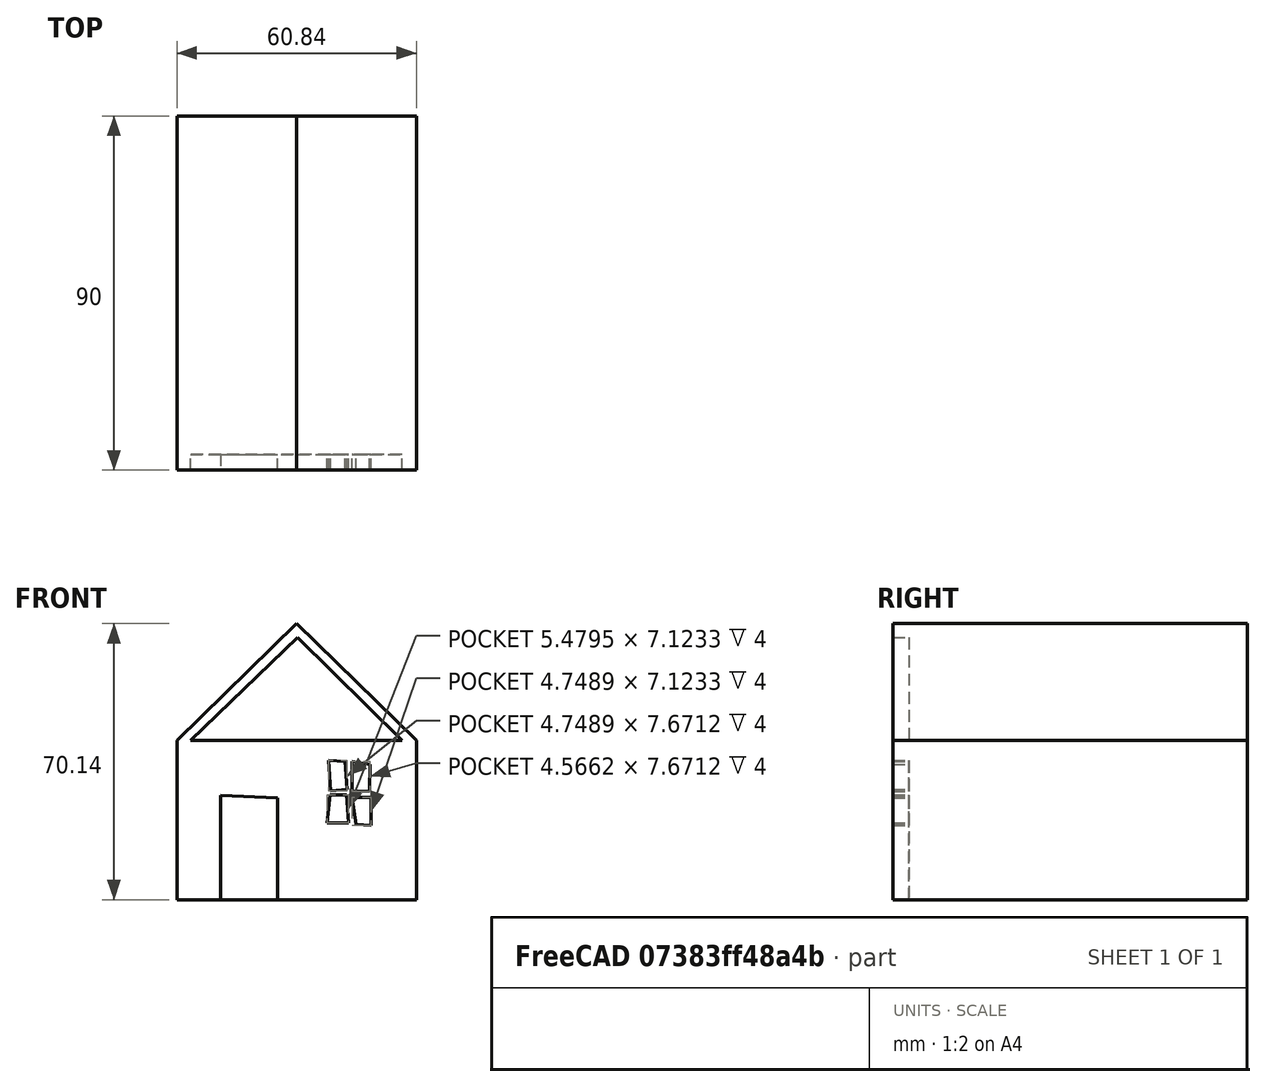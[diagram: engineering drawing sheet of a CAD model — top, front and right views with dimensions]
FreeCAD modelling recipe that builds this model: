
FCSTD DOCUMENT  (FreeCAD 0.21R33694 (Git))
Label: OJT1_T017_R02_caseta
License: All rights reserved
LicenseURL: http://en.wikipedia.org/wiki/All_rights_reserved
objects: PartDesign::SubShapeBinder×5, Sketcher::SketchObject×2, PartDesign::Pad×1, PartDesign::Pocket×1, PartDesign::Body×1
note: 12 computed .brp shape members not serialized (recipe doc carries the construction recipe); baked Part::Feature solids carry a one-line shape summary decoded from their .brp

FEATURE [Sketcher::SketchObject] Sketch
  FullyConstrained = false
  MapMode = 5
  Support = -> [XY_Plane]
  sketch-geometry (5):
    g0: LineSegment StartX=0 StartY=29.646 StartZ=0 EndX=-30.4204 EndY=0 EndZ=0
    g1: LineSegment StartX=-30.4204 StartY=0 StartZ=0 EndX=-30.4204 EndY=-40.4867 EndZ=0
    g2: LineSegment StartX=-30.4204 StartY=-40.4867 StartZ=0 EndX=30.4204 EndY=-40.4867 EndZ=0
    g3: LineSegment StartX=30.4204 StartY=-40.4867 StartZ=0 EndX=30.4204 EndY=0 EndZ=0
    g4: LineSegment StartX=30.4204 StartY=0 StartZ=0 EndX=0 EndY=29.646 EndZ=0
  constraints (11):
    c: PointOnObject(g0,g-2)
    c: PointOnObject(g0,g-1)
    c: Coincident(g0,g1)
    c: Vertical(g1)
    c: Coincident(g1,g2)
    c: Horizontal(g2)
    c: Coincident(g2,g3)
    c: PointOnObject(g3,g-1)
    c: Vertical(g3)
    c: Coincident(g3,g4)
    c: Coincident(g4,g0)
FEATURE [PartDesign::Pad] Pad
  Direction = (0,0,1)
  Length = 90
  Length2 = 10
  Profile = -> Sketch
  ReferenceAxis = -> Sketch [N_Axis]
  Type = 0
FEATURE [Sketcher::SketchObject] Sketch001
  FullyConstrained = false
  MapMode = 5
  Placement = pos=(0,0,90) rot=(0,0,1;0rad)
  Support = -> [Pad]
  sketch-geometry (23):
    g0: LineSegment StartX=-19.3703 StartY=-13.9467 StartZ=0 EndX=-19.3703 EndY=-40.9403 EndZ=0
    g1: LineSegment StartX=-19.3703 StartY=-40.9403 StartZ=0 EndX=-4.86962 EndY=-40.9403 EndZ=0
    g2: LineSegment StartX=-4.86962 StartY=-40.9403 StartZ=0 EndX=-4.86962 EndY=-14.616 EndZ=0
    g3: LineSegment StartX=-4.86962 StartY=-14.616 StartZ=0 EndX=-19.3703 EndY=-13.9467 EndZ=0
    g4: LineSegment StartX=8.11109 StartY=-5.15465 StartZ=0 EndX=8.65904 EndY=-12.8259 EndZ=0
    g5: LineSegment StartX=8.65904 StartY=-12.8259 StartZ=0 EndX=12.86 EndY=-12.4606 EndZ=0
    g6: LineSegment StartX=12.86 StartY=-12.4606 StartZ=0 EndX=12.312 EndY=-5.3373 EndZ=0
    g7: LineSegment StartX=12.312 StartY=-5.3373 StartZ=0 EndX=8.11109 EndY=-5.15465 EndZ=0
    g8: LineSegment StartX=14.1385 StartY=-5.3373 StartZ=0 EndX=14.1385 EndY=-13.0085 EndZ=0
    g9: LineSegment StartX=14.1385 StartY=-13.0085 StartZ=0 EndX=18.5221 EndY=-12.8259 EndZ=0
    g10: LineSegment StartX=18.5221 StartY=-12.8259 StartZ=0 EndX=18.7047 EndY=-6.06789 EndZ=0
    g11: LineSegment StartX=18.7047 StartY=-6.06789 StartZ=0 EndX=14.1385 EndY=-5.3373 EndZ=0
    g12: LineSegment StartX=8.47639 StartY=-13.9218 StartZ=0 EndX=12.6773 EndY=-13.9218 EndZ=0
    g13: LineSegment StartX=12.6773 StartY=-13.9218 StartZ=0 EndX=13.2253 EndY=-21.0451 EndZ=0
    g14: LineSegment StartX=13.2253 StartY=-21.0451 StartZ=0 EndX=7.7458 EndY=-21.0451 EndZ=0
    g15: LineSegment StartX=7.7458 StartY=-21.0451 StartZ=0 EndX=8.47639 EndY=-13.9218 EndZ=0
    g16: LineSegment StartX=14.1385 StartY=-14.4697 StartZ=0 EndX=15.0517 EndY=-21.4104 EndZ=0
    g17: LineSegment StartX=15.0517 StartY=-21.4104 StartZ=0 EndX=18.8874 EndY=-21.593 EndZ=0
    g18: LineSegment StartX=18.8874 StartY=-21.593 StartZ=0 EndX=18.8874 EndY=-14.4697 EndZ=0
    g19: LineSegment StartX=18.8874 StartY=-14.4697 StartZ=0 EndX=14.1385 EndY=-14.4697 EndZ=0
    g20: LineSegment StartX=-26.9664 StartY=3.6e-15 StartZ=0 EndX=0.250248 EndY=26.0984 EndZ=0
    g21: LineSegment StartX=0.250248 StartY=26.0984 StartZ=0 EndX=26.7977 EndY=3.6e-15 EndZ=0
    g22: LineSegment StartX=26.7977 StartY=3.6e-15 StartZ=0 EndX=-26.9664 EndY=3.6e-15 EndZ=0
  constraints (33):
    c: Vertical(g0)
    c: Coincident(g0,g1)
    c: Horizontal(g1)
    c: Coincident(g1,g2)
    c: Vertical(g2)
    c: Coincident(g2,g3)
    c: Coincident(g3,g0)
    c: Coincident(g4,g5)
    c: Coincident(g5,g6)
    c: Coincident(g6,g7)
    c: Coincident(g7,g4)
    c: Vertical(g8)
    c: Coincident(g8,g9)
    c: Coincident(g9,g10)
    c: Coincident(g10,g11)
    c: Coincident(g11,g8)
    c: Horizontal(g12)
    c: Coincident(g12,g13)
    c: Coincident(g13,g14)
    c: Horizontal(g14)
    c: Coincident(g14,g15)
    c: Coincident(g15,g12)
    c: Coincident(g16,g17)
    c: Coincident(g17,g18)
    c: Vertical(g18)
    c: Coincident(g18,g19)
    c: Coincident(g19,g16)
    c: Horizontal(g19)
    c: PointOnObject(g20,g-1)
    c: Coincident(g20,g21)
    c: Coincident(g21,g22)
    c: Coincident(g22,g20)
    c: Horizontal(g22)
FEATURE [PartDesign::Pocket] Pocket
  BaseFeature = -> Pad
  Direction = (0,0,-1)
  Length = 4
  Length2 = 5
  Profile = -> Sketch001
  ReferenceAxis = -> Sketch001 [N_Axis]
  Type = 0
FEATURE [PartDesign::SubShapeBinder] Binder
  BindCopyOnChange = 0
  BindMode = 0
  ClaimChildren = false
  Context = -> Body [Binder.]
  Fuse = false
  MakeFace = true
  OffsetFill = false
  OffsetIntersection = false
  OffsetJoinType = 0
  OffsetOpenResult = false
  PartialLoad = false
  Relative = true
  Support = -> [Pocket[Face35]]
  _Version = 2
FEATURE [PartDesign::SubShapeBinder] Binder001
  BindCopyOnChange = 0
  BindMode = 0
  ClaimChildren = false
  Context = -> Body [Binder001.]
  Fuse = false
  MakeFace = true
  OffsetFill = false
  OffsetIntersection = false
  OffsetJoinType = 0
  OffsetOpenResult = false
  PartialLoad = false
  Relative = true
  Support = -> [Pocket[Face2]]
  _Version = 2
FEATURE [PartDesign::SubShapeBinder] Binder002
  BindCopyOnChange = 0
  BindMode = 0
  ClaimChildren = false
  Context = -> Body [Binder002.]
  Fuse = false
  MakeFace = true
  OffsetFill = false
  OffsetIntersection = false
  OffsetJoinType = 0
  OffsetOpenResult = false
  PartialLoad = false
  Relative = true
  Support = -> [Pocket[Face1]]
  _Version = 2
FEATURE [PartDesign::SubShapeBinder] Binder003
  BindCopyOnChange = 0
  BindMode = 0
  ClaimChildren = false
  Context = -> Body [Binder003.]
  Fuse = false
  MakeFace = true
  OffsetFill = false
  OffsetIntersection = false
  OffsetJoinType = 0
  OffsetOpenResult = false
  PartialLoad = false
  Relative = true
  Support = -> [Pocket[Face30]]
  _Version = 2
FEATURE [PartDesign::SubShapeBinder] Binder004
  BindCopyOnChange = 0
  BindMode = 0
  ClaimChildren = false
  Context = -> Body [Binder004.]
  Fuse = false
  MakeFace = true
  OffsetFill = false
  OffsetIntersection = false
  OffsetJoinType = 0
  OffsetOpenResult = false
  PartialLoad = false
  Relative = true
  Support = -> [Pocket[Face33,Face34,Face31,Face32]]
  _Version = 2
FEATURE [PartDesign::Body] Body
  Group = -> [Sketch,Pad,Sketch001,Pocket,Binder,Binder001,Binder002,Binder003,Binder004]
  Origin = -> Origin
  Placement = pos=(0,0,0) rot=(1,0,0;1.5708rad)
  Tip = -> Pocket
